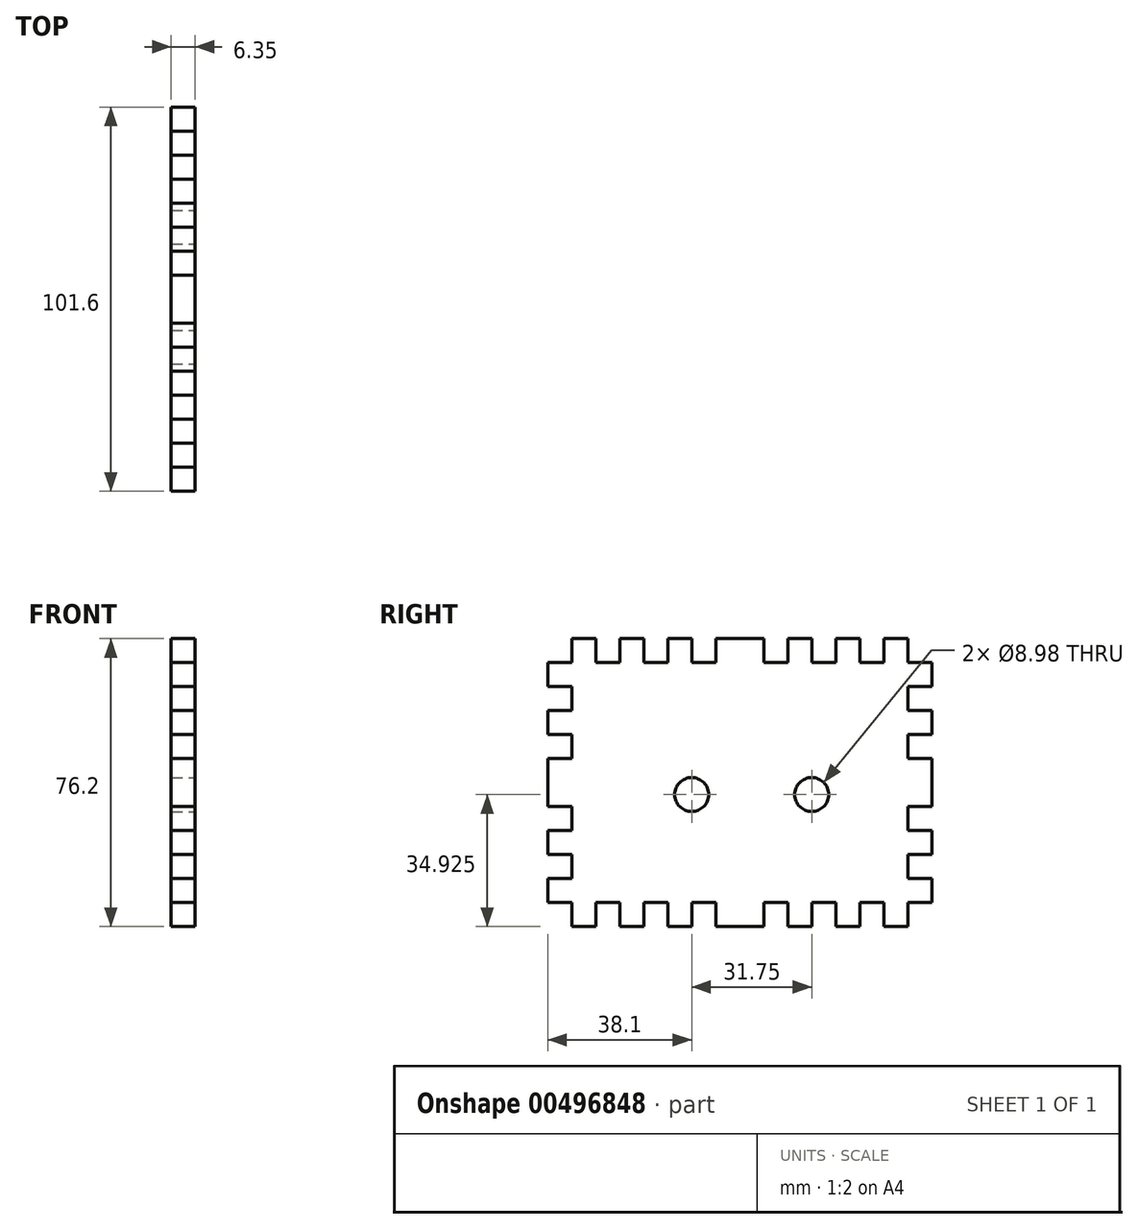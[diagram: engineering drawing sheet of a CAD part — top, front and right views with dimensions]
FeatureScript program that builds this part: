
annotation { "Feature Type Name" : "Feature", "Feature Type Description" : "" }
export const myFeature = defineFeature(function(context is Context, id is Id, definition is map)
    precondition{}
    {
        {
            var Q0;
            Q0=qCreatedBy(makeId("Right.planeOp"),FACE);
            var sketch = newSketch(context, id + "F0", { "sketchPlane" : qUnion([Q0])});
            skLineSegment(sketch, "E0.bottom", {"start": v(-44.45, 38.1) * mm, "end": v(-38.1, 38.1) * mm});
            skLineSegment(sketch, "E0.top", {"start": v(-44.45, -38.1) * mm, "end": v(-38.1, -38.1) * mm});
            skLineSegment(sketch, "E0.left", {"start": v(-50.8, 31.75) * mm, "end": v(-50.8, 25.4) * mm});
            skLineSegment(sketch, "E0.right", {"start": v(50.8, 31.75) * mm, "end": v(50.8, 25.4) * mm});
            skPoint(sketch, "E0.middle", {"position": v(0, 0) * mm});
            skLineSegment(sketch, "E1.top", {"start": v(50.8, 31.75) * mm, "end": v(44.45, 31.75) * mm});
            skLineSegment(sketch, "E1.right", {"start": v(44.45, 38.1) * mm, "end": v(44.45, 31.75) * mm});
            skLineSegment(sketch, "E2.bottom", {"start": v(44.45, 38.1) * mm, "end": v(38.1, 38.1) * mm});
            skLineSegment(sketch, "E2.right", {"start": v(38.1, 38.1) * mm, "end": v(38.1, 31.75) * mm});
            skLineSegment(sketch, "E3.top", {"start": v(38.1, 31.75) * mm, "end": v(31.75, 31.75) * mm});
            skLineSegment(sketch, "E3.right", {"start": v(31.75, 38.1) * mm, "end": v(31.75, 31.75) * mm});
            skLineSegment(sketch, "E4.bottom", {"start": v(31.75, 38.1) * mm, "end": v(25.4, 38.1) * mm});
            skLineSegment(sketch, "E4.right", {"start": v(25.4, 38.1) * mm, "end": v(25.4, 31.75) * mm});
            skPoint(sketch, "E5.oppositeSnap0", {"position": v(34.93, 31.75) * mm});
            skLineSegment(sketch, "E5.top", {"start": v(25.4, 31.75) * mm, "end": v(19.05, 31.75) * mm});
            skLineSegment(sketch, "E5.right", {"start": v(19.05, 38.1) * mm, "end": v(19.05, 31.75) * mm});
            skLineSegment(sketch, "E6.top", {"start": v(19.05, 38.1) * mm, "end": v(12.7, 38.1) * mm});
            skLineSegment(sketch, "E6.left", {"start": v(19.05, 31.75) * mm, "end": v(19.05, 38.1) * mm});
            skLineSegment(sketch, "E6.right", {"start": v(12.7, 31.75) * mm, "end": v(12.7, 38.1) * mm});
            skLineSegment(sketch, "E7.bottom", {"start": v(12.7, 31.75) * mm, "end": v(6.35, 31.75) * mm});
            skLineSegment(sketch, "E7.right", {"start": v(6.35, 31.75) * mm, "end": v(6.35, 38.1) * mm});
            skLineSegment(sketch, "E8.top", {"start": v(6.35, 38.1) * mm, "end": v(0, 38.1) * mm});
            skLineSegment(sketch, "E9.top", {"start": v(0, 38.1) * mm, "end": v(-6.35, 38.1) * mm});
            skLineSegment(sketch, "E9.right", {"start": v(-6.35, 31.75) * mm, "end": v(-6.35, 38.1) * mm});
            skLineSegment(sketch, "E10.bottom", {"start": v(-6.35, 31.75) * mm, "end": v(-12.7, 31.75) * mm});
            skLineSegment(sketch, "E10.right", {"start": v(-12.7, 31.75) * mm, "end": v(-12.7, 38.1) * mm});
            skLineSegment(sketch, "E11.top", {"start": v(-12.7, 38.1) * mm, "end": v(-19.05, 38.1) * mm});
            skLineSegment(sketch, "E11.right", {"start": v(-19.05, 31.75) * mm, "end": v(-19.05, 38.1) * mm});
            skLineSegment(sketch, "E12.bottom", {"start": v(-19.05, 31.75) * mm, "end": v(-25.4, 31.75) * mm});
            skLineSegment(sketch, "E12.right", {"start": v(-25.4, 31.75) * mm, "end": v(-25.4, 38.1) * mm});
            skLineSegment(sketch, "E13.top", {"start": v(-25.4, 38.1) * mm, "end": v(-31.75, 38.1) * mm});
            skLineSegment(sketch, "E13.right", {"start": v(-31.75, 31.75) * mm, "end": v(-31.75, 38.1) * mm});
            skLineSegment(sketch, "E14.bottom", {"start": v(-31.75, 31.75) * mm, "end": v(-38.1, 31.75) * mm});
            skLineSegment(sketch, "E14.right", {"start": v(-38.1, 31.75) * mm, "end": v(-38.1, 38.1) * mm});
            skLineSegment(sketch, "E15.top", {"start": v(-38.1, 38.1) * mm, "end": v(-44.45, 38.1) * mm});
            skLineSegment(sketch, "E15.right", {"start": v(-44.45, 31.75) * mm, "end": v(-44.45, 38.1) * mm});
            skLineSegment(sketch, "E16.bottom", {"start": v(-44.45, 31.75) * mm, "end": v(-50.8, 31.75) * mm});
            skLineSegment(sketch, "E17.bottom", {"start": v(44.45, 31.75) * mm, "end": v(50.8, 31.75) * mm});
            skLineSegment(sketch, "E17.top", {"start": v(44.45, 25.4) * mm, "end": v(50.8, 25.4) * mm});
            skLineSegment(sketch, "E18.top", {"start": v(44.45, 19.05) * mm, "end": v(50.8, 19.05) * mm});
            skLineSegment(sketch, "E18.left", {"start": v(44.45, 25.4) * mm, "end": v(44.45, 19.05) * mm});
            skLineSegment(sketch, "E19.top", {"start": v(44.45, 12.7) * mm, "end": v(50.8, 12.7) * mm});
            skLineSegment(sketch, "E19.right", {"start": v(50.8, 19.05) * mm, "end": v(50.8, 12.7) * mm});
            skLineSegment(sketch, "E20.top", {"start": v(44.45, 6.35) * mm, "end": v(50.8, 6.35) * mm});
            skLineSegment(sketch, "E20.left", {"start": v(44.45, 12.7) * mm, "end": v(44.45, 6.35) * mm});
            skLineSegment(sketch, "E21.right", {"start": v(50.8, 6.35) * mm, "end": v(50.8, 0) * mm});
            skLineSegment(sketch, "E22.top", {"start": v(44.45, -6.35) * mm, "end": v(50.8, -6.35) * mm});
            skLineSegment(sketch, "E22.right", {"start": v(50.8, 0) * mm, "end": v(50.8, -6.35) * mm});
            skLineSegment(sketch, "E23.top", {"start": v(44.45, -12.7) * mm, "end": v(50.8, -12.7) * mm});
            skLineSegment(sketch, "E23.left", {"start": v(44.45, -6.35) * mm, "end": v(44.45, -12.7) * mm});
            skLineSegment(sketch, "E24.top", {"start": v(44.45, -19.05) * mm, "end": v(50.8, -19.05) * mm});
            skLineSegment(sketch, "E24.right", {"start": v(50.8, -12.7) * mm, "end": v(50.8, -19.05) * mm});
            skLineSegment(sketch, "E25.top", {"start": v(44.45, -25.4) * mm, "end": v(50.8, -25.4) * mm});
            skLineSegment(sketch, "E25.left", {"start": v(44.45, -19.05) * mm, "end": v(44.45, -25.4) * mm});
            skLineSegment(sketch, "E26.top", {"start": v(44.45, -31.75) * mm, "end": v(50.8, -31.75) * mm});
            skLineSegment(sketch, "E26.right", {"start": v(50.8, -25.4) * mm, "end": v(50.8, -31.75) * mm});
            skLineSegment(sketch, "E27.left", {"start": v(44.45, -31.75) * mm, "end": v(44.45, -38.1) * mm});
            skLineSegment(sketch, "E28.top", {"start": v(44.45, -38.1) * mm, "end": v(38.1, -38.1) * mm});
            skLineSegment(sketch, "E28.right", {"start": v(38.1, -31.75) * mm, "end": v(38.1, -38.1) * mm});
            skLineSegment(sketch, "E29.bottom", {"start": v(38.1, -31.75) * mm, "end": v(31.75, -31.75) * mm});
            skLineSegment(sketch, "E29.right", {"start": v(31.75, -31.75) * mm, "end": v(31.75, -38.1) * mm});
            skLineSegment(sketch, "E30.top", {"start": v(31.75, -38.1) * mm, "end": v(25.4, -38.1) * mm});
            skLineSegment(sketch, "E30.right", {"start": v(25.4, -31.75) * mm, "end": v(25.4, -38.1) * mm});
            skLineSegment(sketch, "E31.bottom", {"start": v(25.4, -31.75) * mm, "end": v(19.05, -31.75) * mm});
            skLineSegment(sketch, "E31.right", {"start": v(19.05, -31.75) * mm, "end": v(19.05, -38.1) * mm});
            skLineSegment(sketch, "E32.top", {"start": v(19.05, -38.1) * mm, "end": v(12.7, -38.1) * mm});
            skLineSegment(sketch, "E32.right", {"start": v(12.7, -31.75) * mm, "end": v(12.7, -38.1) * mm});
            skLineSegment(sketch, "E33.bottom", {"start": v(12.7, -31.75) * mm, "end": v(6.35, -31.75) * mm});
            skLineSegment(sketch, "E33.right", {"start": v(6.35, -31.75) * mm, "end": v(6.35, -38.1) * mm});
            skLineSegment(sketch, "E34.top", {"start": v(6.35, -38.1) * mm, "end": v(0, -38.1) * mm});
            skLineSegment(sketch, "E35.top", {"start": v(0, -38.1) * mm, "end": v(-6.35, -38.1) * mm});
            skLineSegment(sketch, "E35.right", {"start": v(-6.35, -31.75) * mm, "end": v(-6.35, -38.1) * mm});
            skLineSegment(sketch, "E36.top", {"start": v(-6.35, -31.75) * mm, "end": v(-12.7, -31.75) * mm});
            skLineSegment(sketch, "E36.left", {"start": v(-6.35, -38.1) * mm, "end": v(-6.35, -31.75) * mm});
            skLineSegment(sketch, "E36.right", {"start": v(-12.7, -38.1) * mm, "end": v(-12.7, -31.75) * mm});
            skLineSegment(sketch, "E37.bottom", {"start": v(-12.7, -38.1) * mm, "end": v(-19.05, -38.1) * mm});
            skLineSegment(sketch, "E37.right", {"start": v(-19.05, -38.1) * mm, "end": v(-19.05, -31.75) * mm});
            skLineSegment(sketch, "E38.bottom", {"start": v(-19.05, -31.75) * mm, "end": v(-25.4, -31.75) * mm});
            skLineSegment(sketch, "E38.left", {"start": v(-19.05, -31.75) * mm, "end": v(-19.05, -38.1) * mm});
            skLineSegment(sketch, "E38.right", {"start": v(-25.4, -31.75) * mm, "end": v(-25.4, -38.1) * mm});
            skLineSegment(sketch, "E39.top", {"start": v(-25.4, -38.1) * mm, "end": v(-31.75, -38.1) * mm});
            skLineSegment(sketch, "E39.right", {"start": v(-31.75, -31.75) * mm, "end": v(-31.75, -38.1) * mm});
            skLineSegment(sketch, "E40.top", {"start": v(-31.75, -31.75) * mm, "end": v(-38.1, -31.75) * mm});
            skLineSegment(sketch, "E40.left", {"start": v(-31.75, -38.1) * mm, "end": v(-31.75, -31.75) * mm});
            skLineSegment(sketch, "E40.right", {"start": v(-38.1, -38.1) * mm, "end": v(-38.1, -31.75) * mm});
            skLineSegment(sketch, "E41.bottom", {"start": v(-38.1, -38.1) * mm, "end": v(-44.45, -38.1) * mm});
            skLineSegment(sketch, "E41.right", {"start": v(-44.45, -38.1) * mm, "end": v(-44.45, -31.75) * mm});
            skLineSegment(sketch, "E42.top", {"start": v(-44.45, -31.75) * mm, "end": v(-50.8, -31.75) * mm});
            skLineSegment(sketch, "E43.top", {"start": v(-44.45, 25.4) * mm, "end": v(-50.8, 25.4) * mm});
            skLineSegment(sketch, "E44.top", {"start": v(-44.45, 19.05) * mm, "end": v(-50.8, 19.05) * mm});
            skLineSegment(sketch, "E44.left", {"start": v(-44.45, 25.4) * mm, "end": v(-44.45, 19.05) * mm});
            skLineSegment(sketch, "E45.top", {"start": v(-44.45, 12.7) * mm, "end": v(-50.8, 12.7) * mm});
            skLineSegment(sketch, "E45.right", {"start": v(-50.8, 19.05) * mm, "end": v(-50.8, 12.7) * mm});
            skLineSegment(sketch, "E46.top", {"start": v(-44.45, 6.35) * mm, "end": v(-50.8, 6.35) * mm});
            skLineSegment(sketch, "E46.left", {"start": v(-44.45, 12.7) * mm, "end": v(-44.45, 6.35) * mm});
            skLineSegment(sketch, "E47.right", {"start": v(-50.8, 6.35) * mm, "end": v(-50.8, 0) * mm});
            skLineSegment(sketch, "E48.top", {"start": v(-44.45, -6.35) * mm, "end": v(-50.8, -6.35) * mm});
            skLineSegment(sketch, "E48.right", {"start": v(-50.8, 0) * mm, "end": v(-50.8, -6.35) * mm});
            skLineSegment(sketch, "E49.top", {"start": v(-44.45, -12.7) * mm, "end": v(-50.8, -12.7) * mm});
            skLineSegment(sketch, "E49.left", {"start": v(-44.45, -6.35) * mm, "end": v(-44.45, -12.7) * mm});
            skLineSegment(sketch, "E50.top", {"start": v(-44.45, -19.05) * mm, "end": v(-50.8, -19.05) * mm});
            skLineSegment(sketch, "E50.right", {"start": v(-50.8, -12.7) * mm, "end": v(-50.8, -19.05) * mm});
            skLineSegment(sketch, "E51.top", {"start": v(-44.45, -25.4) * mm, "end": v(-50.8, -25.4) * mm});
            skLineSegment(sketch, "E51.left", {"start": v(-44.45, -19.05) * mm, "end": v(-44.45, -25.4) * mm});
            skLineSegment(sketch, "E52.right", {"start": v(-50.8, -25.4) * mm, "end": v(-50.8, -31.75) * mm});
            skPoint(sketch, "E16.top.end.orphan", {"position": v(-50.8, 38.1) * mm});
            skLineSegment(sketch, "E53.trimOffspring", {"start": v(-31.75, 38.1) * mm, "end": v(-25.4, 38.1) * mm});
            skLineSegment(sketch, "E54.trimOffspring", {"start": v(-19.05, 38.1) * mm, "end": v(-12.7, 38.1) * mm});
            skLineSegment(sketch, "E55.trimOffspring", {"start": v(-6.35, 38.1) * mm, "end": v(6.35, 38.1) * mm});
            skLineSegment(sketch, "E56.trimOffspring", {"start": v(25.4, 38.1) * mm, "end": v(31.75, 38.1) * mm});
            skLineSegment(sketch, "E57.trimOffspring", {"start": v(38.1, 38.1) * mm, "end": v(44.45, 38.1) * mm});
            skPoint(sketch, "E58.orphan", {"position": v(50.8, 38.1) * mm});
            skLineSegment(sketch, "E59.trimOffspring", {"start": v(50.8, 6.35) * mm, "end": v(50.8, -6.35) * mm});
            skLineSegment(sketch, "E60.trimOffspring", {"start": v(-50.8, 6.35) * mm, "end": v(-50.8, -6.35) * mm});
            skPoint(sketch, "E27.top.end.orphan", {"position": v(50.8, -38.1) * mm});
            skLineSegment(sketch, "E61.trimOffspring", {"start": v(38.1, -38.1) * mm, "end": v(44.45, -38.1) * mm});
            skLineSegment(sketch, "E62.trimOffspring", {"start": v(25.4, -38.1) * mm, "end": v(31.75, -38.1) * mm});
            skLineSegment(sketch, "E63.trimOffspring", {"start": v(12.7, -38.1) * mm, "end": v(19.05, -38.1) * mm});
            skLineSegment(sketch, "E64.trimOffspring", {"start": v(0, -38.1) * mm, "end": v(6.35, -38.1) * mm});
            skLineSegment(sketch, "E65.trimOffspring", {"start": v(-19.05, -38.1) * mm, "end": v(-12.7, -38.1) * mm});
            skLineSegment(sketch, "E66.trimOffspring", {"start": v(-31.75, -38.1) * mm, "end": v(-25.4, -38.1) * mm});
            skPoint(sketch, "E67.orphan", {"position": v(-50.8, -38.1) * mm});
            skSolve(sketch);
        }
        {
            var Q0;
            Q0=makeQuery(id+"F0.imprint","IMPRINT",FACE,{"disambiguationData":[TD([[makeQuery(id+"F0.imprint","IMPRINT",EDGE,{"derivedFrom":sQuery(id+"F0.wireOp",EDGE,"E1.right")}),-1.0]])]});
            extrude(context, id + "F1", {"entities" : qUnion([Q0]), "depth" : 6.35 * mm});
        }
        {
            var Q0;
            Q0=makeQuery(id+"F1.opExtrude","CAP_FACE",FACE,{"disambiguationData":[OSD([sQuery(id+"F0.wireOp",EDGE,"E1.right"),sQuery(id+"F0.wireOp",EDGE,"E3.top"),sQuery(id+"F0.wireOp",EDGE,"E2.right"),sQuery(id+"F0.wireOp",EDGE,"E3.right"),sQuery(id+"F0.wireOp",EDGE,"E5.top"),sQuery(id+"F0.wireOp",EDGE,"E4.right"),sQuery(id+"F0.wireOp",EDGE,"E6.top"),sQuery(id+"F0.wireOp",EDGE,"E6.left"),sQuery(id+"F0.wireOp",EDGE,"E7.bottom"),sQuery(id+"F0.wireOp",EDGE,"E6.right"),sQuery(id+"F0.wireOp",EDGE,"E7.right"),sQuery(id+"F0.wireOp",EDGE,"E10.bottom"),sQuery(id+"F0.wireOp",EDGE,"E9.right"),sQuery(id+"F0.wireOp",EDGE,"E10.right"),sQuery(id+"F0.wireOp",EDGE,"E12.bottom"),sQuery(id+"F0.wireOp",EDGE,"E11.right"),sQuery(id+"F0.wireOp",EDGE,"E12.right"),sQuery(id+"F0.wireOp",EDGE,"E14.bottom"),sQuery(id+"F0.wireOp",EDGE,"E13.right"),sQuery(id+"F0.wireOp",EDGE,"E15.top"),sQuery(id+"F0.wireOp",EDGE,"E14.right"),sQuery(id+"F0.wireOp",EDGE,"E15.right"),sQuery(id+"F0.wireOp",EDGE,"E17.bottom"),sQuery(id+"F0.wireOp",EDGE,"E0.right"),sQuery(id+"F0.wireOp",EDGE,"E17.top"),sQuery(id+"F0.wireOp",EDGE,"E18.left"),sQuery(id+"F0.wireOp",EDGE,"E18.top"),sQuery(id+"F0.wireOp",EDGE,"E19.top"),sQuery(id+"F0.wireOp",EDGE,"E20.left"),sQuery(id+"F0.wireOp",EDGE,"E20.top"),sQuery(id+"F0.wireOp",EDGE,"E22.top"),sQuery(id+"F0.wireOp",EDGE,"E23.left"),sQuery(id+"F0.wireOp",EDGE,"E23.top"),sQuery(id+"F0.wireOp",EDGE,"E24.top"),sQuery(id+"F0.wireOp",EDGE,"E25.left"),sQuery(id+"F0.wireOp",EDGE,"E25.top"),sQuery(id+"F0.wireOp",EDGE,"E26.top"),sQuery(id+"F0.wireOp",EDGE,"E27.left"),sQuery(id+"F0.wireOp",EDGE,"E29.bottom"),sQuery(id+"F0.wireOp",EDGE,"E28.right"),sQuery(id+"F0.wireOp",EDGE,"E29.right"),sQuery(id+"F0.wireOp",EDGE,"E31.bottom"),sQuery(id+"F0.wireOp",EDGE,"E30.right"),sQuery(id+"F0.wireOp",EDGE,"E31.right"),sQuery(id+"F0.wireOp",EDGE,"E33.bottom"),sQuery(id+"F0.wireOp",EDGE,"E32.right"),sQuery(id+"F0.wireOp",EDGE,"E33.right"),sQuery(id+"F0.wireOp",EDGE,"E35.top"),sQuery(id+"F0.wireOp",EDGE,"E36.top"),sQuery(id+"F0.wireOp",EDGE,"E36.left"),sQuery(id+"F0.wireOp",EDGE,"E36.right"),sQuery(id+"F0.wireOp",EDGE,"E38.bottom"),sQuery(id+"F0.wireOp",EDGE,"E38.left"),sQuery(id+"F0.wireOp",EDGE,"E38.right"),sQuery(id+"F0.wireOp",EDGE,"E40.top"),sQuery(id+"F0.wireOp",EDGE,"E40.left"),sQuery(id+"F0.wireOp",EDGE,"E41.bottom"),sQuery(id+"F0.wireOp",EDGE,"E40.right"),sQuery(id+"F0.wireOp",EDGE,"E41.right"),sQuery(id+"F0.wireOp",EDGE,"E16.bottom"),sQuery(id+"F0.wireOp",EDGE,"E0.left"),sQuery(id+"F0.wireOp",EDGE,"E43.top"),sQuery(id+"F0.wireOp",EDGE,"E44.left"),sQuery(id+"F0.wireOp",EDGE,"E44.top"),sQuery(id+"F0.wireOp",EDGE,"E45.top"),sQuery(id+"F0.wireOp",EDGE,"E46.left"),sQuery(id+"F0.wireOp",EDGE,"E46.top"),sQuery(id+"F0.wireOp",EDGE,"E48.top"),sQuery(id+"F0.wireOp",EDGE,"E49.left"),sQuery(id+"F0.wireOp",EDGE,"E49.top"),sQuery(id+"F0.wireOp",EDGE,"E50.top"),sQuery(id+"F0.wireOp",EDGE,"E51.left"),sQuery(id+"F0.wireOp",EDGE,"E51.top"),sQuery(id+"F0.wireOp",EDGE,"E42.top"),sQuery(id+"F0.wireOp",EDGE,"E53.trimOffspring"),sQuery(id+"F0.wireOp",EDGE,"E54.trimOffspring"),sQuery(id+"F0.wireOp",EDGE,"E55.trimOffspring"),sQuery(id+"F0.wireOp",EDGE,"E56.trimOffspring"),sQuery(id+"F0.wireOp",EDGE,"E57.trimOffspring"),sQuery(id+"F0.wireOp",EDGE,"E19.right"),sQuery(id+"F0.wireOp",EDGE,"E59.trimOffspring"),sQuery(id+"F0.wireOp",EDGE,"E24.right"),sQuery(id+"F0.wireOp",EDGE,"E26.right"),sQuery(id+"F0.wireOp",EDGE,"E45.right"),sQuery(id+"F0.wireOp",EDGE,"E60.trimOffspring"),sQuery(id+"F0.wireOp",EDGE,"E50.right"),sQuery(id+"F0.wireOp",EDGE,"E52.right"),sQuery(id+"F0.wireOp",EDGE,"E61.trimOffspring"),sQuery(id+"F0.wireOp",EDGE,"E62.trimOffspring"),sQuery(id+"F0.wireOp",EDGE,"E63.trimOffspring"),sQuery(id+"F0.wireOp",EDGE,"E64.trimOffspring"),sQuery(id+"F0.wireOp",EDGE,"E65.trimOffspring"),sQuery(id+"F0.wireOp",EDGE,"E66.trimOffspring")])],"isStart":false});
            var sketch = newSketch(context, id + "F2", { "sketchPlane" : qUnion([Q0])});
            skLineSegment(sketch, "E68", {"start": v(-44.45, -9.53) * mm, "end": v(-12.7, -9.53) * mm});
            skLineSegment(sketch, "E69", {"start": v(44.45, -9.53) * mm, "end": v(19.05, -9.53) * mm});
            skLineSegment(sketch, "E70", {"start": v(-9.53, -31.75) * mm, "end": v(-9.53, -3.17) * mm});
            skLineSegment(sketch, "E71.bottom", {"start": v(-9.53, 0) * mm, "end": v(-15.87, 0) * mm});
            skLineSegment(sketch, "E71.top", {"start": v(-9.53, -6.35) * mm, "end": v(-15.87, -6.35) * mm});
            skLineSegment(sketch, "E71.left", {"start": v(-9.53, 0) * mm, "end": v(-9.53, -6.35) * mm});
            skLineSegment(sketch, "E71.right", {"start": v(-15.87, 0) * mm, "end": v(-15.87, -6.35) * mm});
            skPoint(sketch, "E71.middle", {"position": v(-12.7, -3.17) * mm});
            skLineSegment(sketch, "E72.bottom", {"start": v(15.88, 0) * mm, "end": v(22.23, 0) * mm});
            skLineSegment(sketch, "E72.top", {"start": v(15.88, -6.35) * mm, "end": v(22.23, -6.35) * mm});
            skLineSegment(sketch, "E72.left", {"start": v(15.88, 0) * mm, "end": v(15.88, -6.35) * mm});
            skLineSegment(sketch, "E72.right", {"start": v(22.23, 0) * mm, "end": v(22.23, -6.35) * mm});
            skPoint(sketch, "E72.middle", {"position": v(19.05, -3.17) * mm});
            skCircle(sketch, "E73", {"center": v(-12.7, -3.17) * mm, "radius": 4.5 * mm});
            skCircle(sketch, "E74", {"center": v(19.05, -3.17) * mm, "radius": 4.5 * mm});
            skSolve(sketch);
        }
        {
            var Q0;
            {var subQ0=sQuery(id+"F2.wireOp",EDGE,"E71.bottom");Q0=makeQuery(id+"F2.imprint","IMPRINT",FACE,{"disambiguationData":[TD([[makeQuery(id+"F2.imprint","IMPRINT",EDGE,{"derivedFrom":subQ0}),-1.0]])]});}
            var Q1;
            {var subQ4=sQuery(id+"F2.wireOp",EDGE,"E71.bottom");Q1=makeQuery(id+"F2.imprint","IMPRINT",FACE,{"disambiguationData":[TD([[makeQuery(id+"F2.imprint","IMPRINT",EDGE,{"derivedFrom":subQ4}),1.0]])]});}
            var Q2;
            {var subQ0=sQuery(id+"F2.wireOp",EDGE,"E71.right");Q2=makeQuery(id+"F2.imprint","IMPRINT",FACE,{"disambiguationData":[TD([[makeQuery(id+"F2.imprint","IMPRINT",EDGE,{"derivedFrom":subQ0}),-1.0]])]});}
            var Q3;
            {var subQ0=sQuery(id+"F2.wireOp",EDGE,"E71.top");Q3=makeQuery(id+"F2.imprint","IMPRINT",FACE,{"disambiguationData":[TD([[makeQuery(id+"F2.imprint","IMPRINT",EDGE,{"derivedFrom":subQ0}),1.0]])]});}
            var Q4;
            {var subQ1=sQuery(id+"F2.wireOp",EDGE,"E71.left");var subQ3=makeQuery(id+"F2.imprint","IMPRINT",VERTEX,{"derivedFrom":subQ1});Q4=makeQuery(id+"F2.imprint","IMPRINT",FACE,{"disambiguationData":[TD([[makeQuery(id+"F2.imprint","IMPRINT",EDGE,{"disambiguationData":[TD([[subQ3,1.0]])],"derivedFrom":subQ1}),1.0]])]});}
            var Q5;
            Q5=makeQuery(id+"F2.imprint","IMPRINT",FACE,{"disambiguationData":[TD([[makeQuery(id+"F2.imprint","IMPRINT",EDGE,{"derivedFrom":sQuery(id+"F2.wireOp",EDGE,"E72.bottom")}),-1.0]])]});
            var Q6;
            {var subQ0=sQuery(id+"F2.wireOp",EDGE,"E72.bottom");Q6=makeQuery(id+"F2.imprint","IMPRINT",FACE,{"disambiguationData":[TD([[makeQuery(id+"F2.imprint","IMPRINT",EDGE,{"derivedFrom":subQ0}),1.0]])]});}
            var Q7;
            {var subQ0=sQuery(id+"F2.wireOp",EDGE,"E72.left");Q7=makeQuery(id+"F2.imprint","IMPRINT",FACE,{"disambiguationData":[TD([[makeQuery(id+"F2.imprint","IMPRINT",EDGE,{"derivedFrom":subQ0}),-1.0]])]});}
            var Q8;
            {var subQ0=sQuery(id+"F2.wireOp",EDGE,"E72.top");Q8=makeQuery(id+"F2.imprint","IMPRINT",FACE,{"disambiguationData":[TD([[makeQuery(id+"F2.imprint","IMPRINT",EDGE,{"derivedFrom":subQ0}),-1.0]])]});}
            var Q9;
            {var subQ0=sQuery(id+"F2.wireOp",EDGE,"E72.right");Q9=makeQuery(id+"F2.imprint","IMPRINT",FACE,{"disambiguationData":[TD([[makeQuery(id+"F2.imprint","IMPRINT",EDGE,{"derivedFrom":subQ0}),1.0]])]});}
            extrude(context, id + "F3", {"entities" : qUnion([Q0, Q1, Q2, Q3, Q4, Q5, Q6, Q7, Q8, Q9]), "operationType" : NewBodyOperationType.REMOVE, "endBound" : BoundingType.THROUGH_ALL, "oppositeDirection" : true, "depth" : 25.4 * mm});
        }
    });
